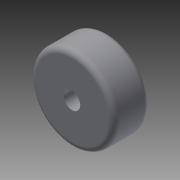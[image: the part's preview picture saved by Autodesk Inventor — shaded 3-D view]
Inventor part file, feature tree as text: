
AUTODESK INVENTOR PART (.ipt)
format: ipt  version: 2013 (Build 170138000, 138)  size: 111,104 bytes
history: native  units: in
note: dims shown in document units (in); Inventor stores cm internally (conversion verified against a paired STEP export)
features: extrude x2, sketch x2, fillet x1
ambient origin geometry x8: Origin, YZ Plane, XZ Plane, XY Plane, X Axis, Y Axis, Z Axis, Center Point
bodies: Solid1 (feature_tree)
feature tree (5):
  extrude  "Extrusion1"  Depth=0.8125in TaperAngle=0.0deg
  extrude  "Extrusion2"  Depth=0.5in TaperAngle=0.0deg
  fillet  "Fillet1"  Radius=0.125in
  sketch  "Sketch1"  dims[d0=1.875in d1=0.8125in d2=0.0in]
  sketch  "Sketch2"  dims[d3=0.375in d4=0.5in d5=0.0in d6=0.125in]
